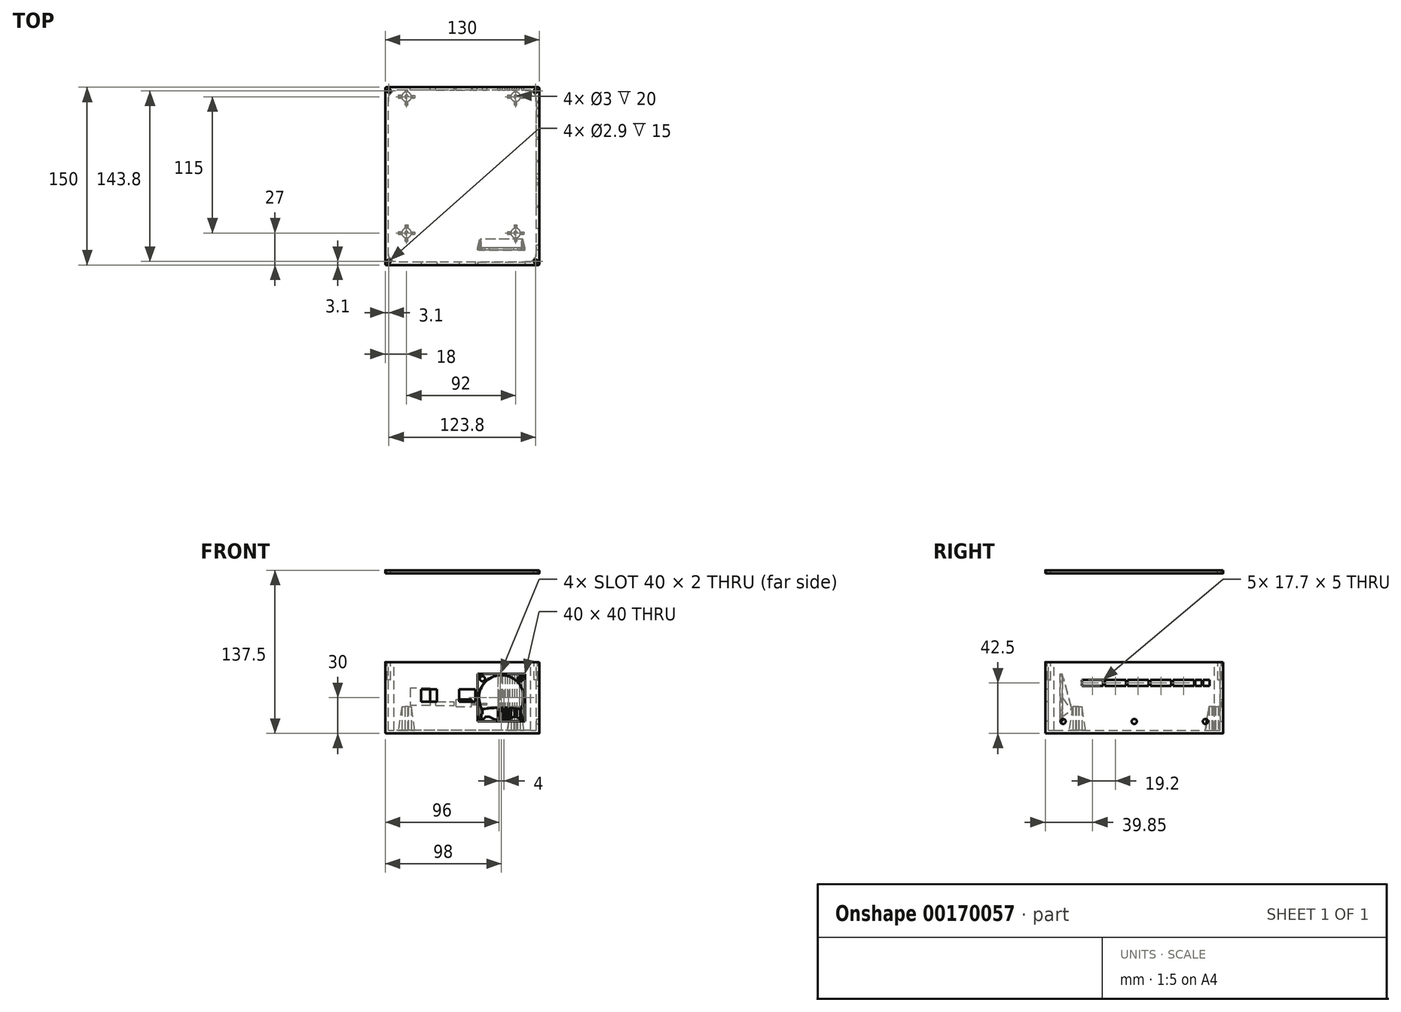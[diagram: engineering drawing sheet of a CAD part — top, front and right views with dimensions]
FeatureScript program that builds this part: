
annotation { "Feature Type Name" : "Feature", "Feature Type Description" : "" }
export const myFeature = defineFeature(function(context is Context, id is Id, definition is map)
    precondition{}
    {
        {
            var Q0;
            Q0=qCreatedBy(makeId("Top.planeOp"),FACE);
            var sketch = newSketch(context, id + "F0", { "sketchPlane" : qUnion([Q0])});
            skLineSegment(sketch, "E0.bottom", {"start": v(65, -75) * mm, "end": v(-65, -75) * mm});
            skLineSegment(sketch, "E0.top", {"start": v(65, 75) * mm, "end": v(-65, 75) * mm});
            skLineSegment(sketch, "E0.left", {"start": v(65, -75) * mm, "end": v(65, 75) * mm});
            skLineSegment(sketch, "E0.right", {"start": v(-65, -75) * mm, "end": v(-65, 75) * mm});
            skPoint(sketch, "E0.middle", {"position": v(0, 0) * mm});
            skCircle(sketch, "E1", {"center": v(-47, 67) * mm, "radius": 1.5 * mm});
            skCircle(sketch, "E2", {"center": v(45, 67) * mm, "radius": 1.5 * mm});
            skCircle(sketch, "E3", {"center": v(45, -48) * mm, "radius": 1.5 * mm});
            skCircle(sketch, "E4", {"center": v(-47, -48) * mm, "radius": 1.5 * mm});
            skCircle(sketch, "E5", {"center": v(-47, -48) * mm, "radius": 4 * mm});
            skCircle(sketch, "E6", {"center": v(45, -48) * mm, "radius": 4 * mm});
            skCircle(sketch, "E7", {"center": v(45, 67) * mm, "radius": 4 * mm});
            skCircle(sketch, "E8", {"center": v(-47, 67) * mm, "radius": 4 * mm});
            skLineSegment(sketch, "E9.bottom", {"start": v(46, 74) * mm, "end": v(44, 74) * mm});
            skLineSegment(sketch, "E9.top", {"start": v(46, 60) * mm, "end": v(44, 60) * mm});
            skLineSegment(sketch, "E9.left", {"start": v(46, 74) * mm, "end": v(46, 70.87) * mm});
            skLineSegment(sketch, "E9.right", {"start": v(44, 74) * mm, "end": v(44, 70.87) * mm});
            skLineSegment(sketch, "E10.bottom", {"start": v(52, 66) * mm, "end": v(48.87, 66) * mm});
            skLineSegment(sketch, "E10.top", {"start": v(52, 68) * mm, "end": v(48.87, 68) * mm});
            skLineSegment(sketch, "E10.left", {"start": v(52, 66) * mm, "end": v(52, 68) * mm});
            skLineSegment(sketch, "E10.right", {"start": v(38, 66) * mm, "end": v(38, 68) * mm});
            skLineSegment(sketch, "E11.trimOffspring", {"start": v(41.13, 68) * mm, "end": v(38, 68) * mm});
            skLineSegment(sketch, "E12.trimOffspring", {"start": v(41.13, 66) * mm, "end": v(38, 66) * mm});
            skLineSegment(sketch, "E13.trimOffspring", {"start": v(44, 63.13) * mm, "end": v(44, 60) * mm});
            skLineSegment(sketch, "E14.trimOffspring", {"start": v(46, 63.13) * mm, "end": v(46, 60) * mm});
            skLineSegment(sketch, "E15.bottom", {"start": v(-40, 66) * mm, "end": v(-43.13, 66) * mm});
            skLineSegment(sketch, "E15.top", {"start": v(-40, 68) * mm, "end": v(-43.13, 68) * mm});
            skLineSegment(sketch, "E15.left", {"start": v(-40, 66) * mm, "end": v(-40, 68) * mm});
            skLineSegment(sketch, "E15.right", {"start": v(-54, 66) * mm, "end": v(-54, 68) * mm});
            skLineSegment(sketch, "E16.bottom", {"start": v(-46, 74) * mm, "end": v(-48, 74) * mm});
            skLineSegment(sketch, "E16.top", {"start": v(-46, 60) * mm, "end": v(-48, 60) * mm});
            skLineSegment(sketch, "E16.left", {"start": v(-46, 74) * mm, "end": v(-46, 70.87) * mm});
            skLineSegment(sketch, "E16.right", {"start": v(-48, 74) * mm, "end": v(-48, 70.87) * mm});
            skLineSegment(sketch, "E17.trimOffspring", {"start": v(-50.87, 68) * mm, "end": v(-54, 68) * mm});
            skLineSegment(sketch, "E18.trimOffspring", {"start": v(-50.87, 66) * mm, "end": v(-54, 66) * mm});
            skLineSegment(sketch, "E19.trimOffspring", {"start": v(-48, 63.13) * mm, "end": v(-48, 60) * mm});
            skLineSegment(sketch, "E20.trimOffspring", {"start": v(-46, 63.13) * mm, "end": v(-46, 60) * mm});
            skLineSegment(sketch, "E21.bottom", {"start": v(-40, -49) * mm, "end": v(-43.13, -49) * mm});
            skLineSegment(sketch, "E21.top", {"start": v(-40, -47) * mm, "end": v(-43.13, -47) * mm});
            skLineSegment(sketch, "E21.left", {"start": v(-40, -49) * mm, "end": v(-40, -47) * mm});
            skLineSegment(sketch, "E21.right", {"start": v(-54, -49) * mm, "end": v(-54, -47) * mm});
            skLineSegment(sketch, "E22.bottom", {"start": v(-46, -41) * mm, "end": v(-48, -41) * mm});
            skLineSegment(sketch, "E22.top", {"start": v(-46, -55) * mm, "end": v(-48, -55) * mm});
            skLineSegment(sketch, "E22.left", {"start": v(-46, -41) * mm, "end": v(-46, -44.13) * mm});
            skLineSegment(sketch, "E22.right", {"start": v(-48, -41) * mm, "end": v(-48, -44.13) * mm});
            skLineSegment(sketch, "E23.trimOffspring", {"start": v(-50.87, -49) * mm, "end": v(-54, -49) * mm});
            skLineSegment(sketch, "E24.trimOffspring", {"start": v(-50.87, -47) * mm, "end": v(-54, -47) * mm});
            skLineSegment(sketch, "E25.trimOffspring", {"start": v(-46, -51.87) * mm, "end": v(-46, -55) * mm});
            skLineSegment(sketch, "E26.trimOffspring", {"start": v(-48, -51.87) * mm, "end": v(-48, -55) * mm});
            skLineSegment(sketch, "E27.bottom", {"start": v(52, -49) * mm, "end": v(48.87, -49) * mm});
            skLineSegment(sketch, "E27.top", {"start": v(52, -47) * mm, "end": v(48.87, -47) * mm});
            skLineSegment(sketch, "E27.left", {"start": v(52, -49) * mm, "end": v(52, -47) * mm});
            skLineSegment(sketch, "E27.right", {"start": v(38, -49) * mm, "end": v(38, -47) * mm});
            skLineSegment(sketch, "E28.bottom", {"start": v(46, -55) * mm, "end": v(44, -55) * mm});
            skLineSegment(sketch, "E28.top", {"start": v(46, -41) * mm, "end": v(44, -41) * mm});
            skLineSegment(sketch, "E28.left", {"start": v(46, -55) * mm, "end": v(46, -51.87) * mm});
            skLineSegment(sketch, "E28.right", {"start": v(44, -55) * mm, "end": v(44, -51.87) * mm});
            skLineSegment(sketch, "E29.trimOffspring", {"start": v(41.13, -49) * mm, "end": v(38, -49) * mm});
            skLineSegment(sketch, "E30.trimOffspring", {"start": v(41.13, -47) * mm, "end": v(38, -47) * mm});
            skLineSegment(sketch, "E31.trimOffspring", {"start": v(44, -44.13) * mm, "end": v(44, -41) * mm});
            skLineSegment(sketch, "E32.trimOffspring", {"start": v(46, -44.13) * mm, "end": v(46, -41) * mm});
            skLineSegment(sketch, "E33", {"start": v(65, 65) * mm, "end": v(55, 75) * mm});
            skLineSegment(sketch, "E34", {"start": v(65, -65) * mm, "end": v(55, -75) * mm});
            skLineSegment(sketch, "E35", {"start": v(-55, 75) * mm, "end": v(-65, 65) * mm});
            skLineSegment(sketch, "E36", {"start": v(-65, -65) * mm, "end": v(-55, -75) * mm});
            skSolve(sketch);
        }
        {
            var Q0;
            Q0=makeQuery(id+"F0.imprint","IMPRINT",FACE,{"disambiguationData":[TD([[makeQuery(id+"F0.imprint","IMPRINT",EDGE,{"derivedFrom":sQuery(id+"F0.wireOp",EDGE,"E0.bottom")}),-1.0]])]});
            var Q1;
            Q1=makeQuery(id+"F0.imprint","IMPRINT",FACE,{"disambiguationData":[TD([[makeQuery(id+"F0.imprint","IMPRINT",EDGE,{"derivedFrom":sQuery(id+"F0.wireOp",EDGE,"E2")}),-1.0]])]});
            var Q2;
            Q2=makeQuery(id+"F0.imprint","IMPRINT",FACE,{"disambiguationData":[TD([[makeQuery(id+"F0.imprint","IMPRINT",EDGE,{"derivedFrom":sQuery(id+"F0.wireOp",EDGE,"E4")}),-1.0]])]});
            var Q3;
            Q3=makeQuery(id+"F0.imprint","IMPRINT",FACE,{"disambiguationData":[TD([[makeQuery(id+"F0.imprint","IMPRINT",EDGE,{"derivedFrom":sQuery(id+"F0.wireOp",EDGE,"E16.top")}),-1.0]])]});
            var Q4;
            Q4=makeQuery(id+"F0.imprint","IMPRINT",FACE,{"disambiguationData":[TD([[makeQuery(id+"F0.imprint","IMPRINT",EDGE,{"derivedFrom":sQuery(id+"F0.wireOp",EDGE,"E21.right")}),-1.0]])]});
            var Q5;
            Q5=makeQuery(id+"F0.imprint","IMPRINT",FACE,{"disambiguationData":[TD([[makeQuery(id+"F0.imprint","IMPRINT",EDGE,{"derivedFrom":sQuery(id+"F0.wireOp",EDGE,"E22.top")}),-1.0]])]});
            var Q6;
            Q6=makeQuery(id+"F0.imprint","IMPRINT",FACE,{"disambiguationData":[TD([[makeQuery(id+"F0.imprint","IMPRINT",EDGE,{"derivedFrom":sQuery(id+"F0.wireOp",EDGE,"E1")}),-1.0]])]});
            var Q7;
            Q7=makeQuery(id+"F0.imprint","IMPRINT",FACE,{"disambiguationData":[TD([[makeQuery(id+"F0.imprint","IMPRINT",EDGE,{"derivedFrom":sQuery(id+"F0.wireOp",EDGE,"E3")}),-1.0]])]});
            var Q8;
            Q8=makeQuery(id+"F0.imprint","IMPRINT",FACE,{"disambiguationData":[TD([[makeQuery(id+"F0.imprint","IMPRINT",EDGE,{"derivedFrom":sQuery(id+"F0.wireOp",EDGE,"E15.right")}),-1.0]])]});
            var Q9;
            Q9=makeQuery(id+"F0.imprint","IMPRINT",FACE,{"disambiguationData":[TD([[makeQuery(id+"F0.imprint","IMPRINT",EDGE,{"derivedFrom":sQuery(id+"F0.wireOp",EDGE,"E28.bottom")}),-1.0]])]});
            var Q10;
            {var subQ0=sQuery(id+"F0.wireOp",EDGE,"E10.bottom");Q10=makeQuery(id+"F0.imprint","IMPRINT",FACE,{"disambiguationData":[TD([[makeQuery(id+"F0.imprint","IMPRINT",EDGE,{"derivedFrom":subQ0}),-1.0]])]});}
            var Q11;
            Q11=makeQuery(id+"F0.imprint","IMPRINT",FACE,{"disambiguationData":[TD([[makeQuery(id+"F0.imprint","IMPRINT",EDGE,{"derivedFrom":sQuery(id+"F0.wireOp",EDGE,"E9.top")}),-1.0]])]});
            var Q12;
            {var subQ0=sQuery(id+"F0.wireOp",EDGE,"E21.bottom");Q12=makeQuery(id+"F0.imprint","IMPRINT",FACE,{"disambiguationData":[TD([[makeQuery(id+"F0.imprint","IMPRINT",EDGE,{"derivedFrom":subQ0}),-1.0]])]});}
            var Q13;
            Q13=makeQuery(id+"F0.imprint","IMPRINT",FACE,{"disambiguationData":[TD([[makeQuery(id+"F0.imprint","IMPRINT",EDGE,{"derivedFrom":sQuery(id+"F0.wireOp",EDGE,"E28.top")}),1.0]])]});
            var Q14;
            Q14=makeQuery(id+"F0.imprint","IMPRINT",FACE,{"disambiguationData":[TD([[makeQuery(id+"F0.imprint","IMPRINT",EDGE,{"derivedFrom":sQuery(id+"F0.wireOp",EDGE,"E27.right")}),-1.0]])]});
            var Q15;
            Q15=makeQuery(id+"F0.imprint","IMPRINT",FACE,{"disambiguationData":[TD([[makeQuery(id+"F0.imprint","IMPRINT",EDGE,{"derivedFrom":sQuery(id+"F0.wireOp",EDGE,"E22.bottom")}),1.0]])]});
            var Q16;
            {var subQ0=sQuery(id+"F0.wireOp",EDGE,"E15.bottom");Q16=makeQuery(id+"F0.imprint","IMPRINT",FACE,{"disambiguationData":[TD([[makeQuery(id+"F0.imprint","IMPRINT",EDGE,{"derivedFrom":subQ0}),-1.0]])]});}
            var Q17;
            Q17=makeQuery(id+"F0.imprint","IMPRINT",FACE,{"disambiguationData":[TD([[makeQuery(id+"F0.imprint","IMPRINT",EDGE,{"derivedFrom":sQuery(id+"F0.wireOp",EDGE,"E9.bottom")}),1.0]])]});
            var Q18;
            {var subQ0=sQuery(id+"F0.wireOp",EDGE,"E27.bottom");Q18=makeQuery(id+"F0.imprint","IMPRINT",FACE,{"disambiguationData":[TD([[makeQuery(id+"F0.imprint","IMPRINT",EDGE,{"derivedFrom":subQ0}),-1.0]])]});}
            var Q19;
            Q19=makeQuery(id+"F0.imprint","IMPRINT",FACE,{"disambiguationData":[TD([[makeQuery(id+"F0.imprint","IMPRINT",EDGE,{"derivedFrom":sQuery(id+"F0.wireOp",EDGE,"E10.right")}),-1.0]])]});
            var Q20;
            Q20=makeQuery(id+"F0.imprint","IMPRINT",FACE,{"disambiguationData":[TD([[makeQuery(id+"F0.imprint","IMPRINT",EDGE,{"derivedFrom":sQuery(id+"F0.wireOp",EDGE,"E16.bottom")}),1.0]])]});
            var Q21;
            Q21=makeQuery(id+"F0.imprint","IMPRINT",FACE,{"disambiguationData":[TD([[makeQuery(id+"F0.imprint","IMPRINT",EDGE,{"derivedFrom":sQuery(id+"F0.wireOp",EDGE,"E2")}),1.0]])]});
            var Q22;
            Q22=makeQuery(id+"F0.imprint","IMPRINT",FACE,{"disambiguationData":[TD([[makeQuery(id+"F0.imprint","IMPRINT",EDGE,{"derivedFrom":sQuery(id+"F0.wireOp",EDGE,"E1")}),1.0]])]});
            var Q23;
            Q23=makeQuery(id+"F0.imprint","IMPRINT",FACE,{"disambiguationData":[TD([[makeQuery(id+"F0.imprint","IMPRINT",EDGE,{"derivedFrom":sQuery(id+"F0.wireOp",EDGE,"E4")}),1.0]])]});
            var Q24;
            Q24=makeQuery(id+"F0.imprint","IMPRINT",FACE,{"disambiguationData":[TD([[makeQuery(id+"F0.imprint","IMPRINT",EDGE,{"derivedFrom":sQuery(id+"F0.wireOp",EDGE,"E3")}),1.0]])]});
            var Q25;
            Q25=makeQuery(id+"F0.imprint","IMPRINT",FACE,{"disambiguationData":[TD([[makeQuery(id+"F0.imprint","IMPRINT",EDGE,{"derivedFrom":sQuery(id+"F0.wireOp",EDGE,"E9.bottom")}),-1.0]])]});
            var Q26;
            {var subQ3=sQuery(id+"F0.wireOp",EDGE,"E33");Q26=makeQuery(id+"F0.imprint","IMPRINT",FACE,{"disambiguationData":[TD([[makeQuery(id+"F0.imprint","IMPRINT",EDGE,{"derivedFrom":subQ3}),-1.0]])]});}
            var Q27;
            {var subQ3=sQuery(id+"F0.wireOp",EDGE,"E35");Q27=makeQuery(id+"F0.imprint","IMPRINT",FACE,{"disambiguationData":[TD([[makeQuery(id+"F0.imprint","IMPRINT",EDGE,{"derivedFrom":subQ3}),-1.0]])]});}
            extrude(context, id + "F1", {"entities" : qUnion([Q0, Q1, Q2, Q3, Q4, Q5, Q6, Q7, Q8, Q9, Q10, Q11, Q12, Q13, Q14, Q15, Q16, Q17, Q18, Q19, Q20, Q21, Q22, Q23, Q24, Q25, Q26, Q27]), "depth" : 60 * mm});
        }
        {
            var Q0;
            Q0=makeQuery(id+"F1.opExtrude","CAP_FACE",FACE,{"disambiguationData":[OSD([sQuery(id+"F0.wireOp",EDGE,"E0.bottom"),sQuery(id+"F0.wireOp",EDGE,"E0.top"),sQuery(id+"F0.wireOp",EDGE,"E0.left"),sQuery(id+"F0.wireOp",EDGE,"E0.right")])],"isStart":false});
            shell(context, id + "F2", {"entities" : qUnion([Q0]), "thickness" : 2.5 * mm});
        }
        {
            var Q0;
            Q0=makeQuery(id+"F0.imprint","IMPRINT",FACE,{"disambiguationData":[TD([[makeQuery(id+"F0.imprint","IMPRINT",EDGE,{"derivedFrom":sQuery(id+"F0.wireOp",EDGE,"E1")}),-1.0]])]});
            var Q1;
            Q1=makeQuery(id+"F0.imprint","IMPRINT",FACE,{"disambiguationData":[TD([[makeQuery(id+"F0.imprint","IMPRINT",EDGE,{"derivedFrom":sQuery(id+"F0.wireOp",EDGE,"E4")}),-1.0]])]});
            var Q2;
            Q2=makeQuery(id+"F0.imprint","IMPRINT",FACE,{"disambiguationData":[TD([[makeQuery(id+"F0.imprint","IMPRINT",EDGE,{"derivedFrom":sQuery(id+"F0.wireOp",EDGE,"E3")}),-1.0]])]});
            var Q3;
            Q3=makeQuery(id+"F0.imprint","IMPRINT",FACE,{"disambiguationData":[TD([[makeQuery(id+"F0.imprint","IMPRINT",EDGE,{"derivedFrom":sQuery(id+"F0.wireOp",EDGE,"E2")}),-1.0]])]});
            var Q4;
            {var subQ0=sQuery(id+"F0.wireOp",EDGE,"E10.bottom");Q4=makeQuery(id+"F0.imprint","IMPRINT",FACE,{"disambiguationData":[TD([[makeQuery(id+"F0.imprint","IMPRINT",EDGE,{"derivedFrom":subQ0}),-1.0]])]});}
            var Q5;
            Q5=makeQuery(id+"F0.imprint","IMPRINT",FACE,{"disambiguationData":[TD([[makeQuery(id+"F0.imprint","IMPRINT",EDGE,{"derivedFrom":sQuery(id+"F0.wireOp",EDGE,"E9.top")}),-1.0]])]});
            var Q6;
            Q6=makeQuery(id+"F0.imprint","IMPRINT",FACE,{"disambiguationData":[TD([[makeQuery(id+"F0.imprint","IMPRINT",EDGE,{"derivedFrom":sQuery(id+"F0.wireOp",EDGE,"E10.right")}),-1.0]])]});
            var Q7;
            Q7=makeQuery(id+"F0.imprint","IMPRINT",FACE,{"disambiguationData":[TD([[makeQuery(id+"F0.imprint","IMPRINT",EDGE,{"derivedFrom":sQuery(id+"F0.wireOp",EDGE,"E9.bottom")}),1.0]])]});
            var Q8;
            Q8=makeQuery(id+"F0.imprint","IMPRINT",FACE,{"disambiguationData":[TD([[makeQuery(id+"F0.imprint","IMPRINT",EDGE,{"derivedFrom":sQuery(id+"F0.wireOp",EDGE,"E16.bottom")}),1.0]])]});
            var Q9;
            Q9=makeQuery(id+"F0.imprint","IMPRINT",FACE,{"disambiguationData":[TD([[makeQuery(id+"F0.imprint","IMPRINT",EDGE,{"derivedFrom":sQuery(id+"F0.wireOp",EDGE,"E15.right")}),-1.0]])]});
            var Q10;
            Q10=makeQuery(id+"F0.imprint","IMPRINT",FACE,{"disambiguationData":[TD([[makeQuery(id+"F0.imprint","IMPRINT",EDGE,{"derivedFrom":sQuery(id+"F0.wireOp",EDGE,"E16.top")}),-1.0]])]});
            var Q11;
            {var subQ0=sQuery(id+"F0.wireOp",EDGE,"E15.bottom");Q11=makeQuery(id+"F0.imprint","IMPRINT",FACE,{"disambiguationData":[TD([[makeQuery(id+"F0.imprint","IMPRINT",EDGE,{"derivedFrom":subQ0}),-1.0]])]});}
            var Q12;
            {var subQ0=sQuery(id+"F0.wireOp",EDGE,"E21.bottom");Q12=makeQuery(id+"F0.imprint","IMPRINT",FACE,{"disambiguationData":[TD([[makeQuery(id+"F0.imprint","IMPRINT",EDGE,{"derivedFrom":subQ0}),-1.0]])]});}
            var Q13;
            Q13=makeQuery(id+"F0.imprint","IMPRINT",FACE,{"disambiguationData":[TD([[makeQuery(id+"F0.imprint","IMPRINT",EDGE,{"derivedFrom":sQuery(id+"F0.wireOp",EDGE,"E22.bottom")}),1.0]])]});
            var Q14;
            Q14=makeQuery(id+"F0.imprint","IMPRINT",FACE,{"disambiguationData":[TD([[makeQuery(id+"F0.imprint","IMPRINT",EDGE,{"derivedFrom":sQuery(id+"F0.wireOp",EDGE,"E21.right")}),-1.0]])]});
            var Q15;
            Q15=makeQuery(id+"F0.imprint","IMPRINT",FACE,{"disambiguationData":[TD([[makeQuery(id+"F0.imprint","IMPRINT",EDGE,{"derivedFrom":sQuery(id+"F0.wireOp",EDGE,"E22.top")}),-1.0]])]});
            var Q16;
            Q16=makeQuery(id+"F0.imprint","IMPRINT",FACE,{"disambiguationData":[TD([[makeQuery(id+"F0.imprint","IMPRINT",EDGE,{"derivedFrom":sQuery(id+"F0.wireOp",EDGE,"E27.right")}),-1.0]])]});
            var Q17;
            Q17=makeQuery(id+"F0.imprint","IMPRINT",FACE,{"disambiguationData":[TD([[makeQuery(id+"F0.imprint","IMPRINT",EDGE,{"derivedFrom":sQuery(id+"F0.wireOp",EDGE,"E28.top")}),1.0]])]});
            var Q18;
            {var subQ0=sQuery(id+"F0.wireOp",EDGE,"E27.bottom");Q18=makeQuery(id+"F0.imprint","IMPRINT",FACE,{"disambiguationData":[TD([[makeQuery(id+"F0.imprint","IMPRINT",EDGE,{"derivedFrom":subQ0}),-1.0]])]});}
            var Q19;
            Q19=makeQuery(id+"F0.imprint","IMPRINT",FACE,{"disambiguationData":[TD([[makeQuery(id+"F0.imprint","IMPRINT",EDGE,{"derivedFrom":sQuery(id+"F0.wireOp",EDGE,"E28.bottom")}),-1.0]])]});
            extrude(context, id + "F3", {"entities" : qUnion([Q0, Q1, Q2, Q3, Q4, Q5, Q6, Q7, Q8, Q9, Q10, Q11, Q12, Q13, Q14, Q15, Q16, Q17, Q18, Q19]), "operationType" : NewBodyOperationType.ADD, "depth" : (20 + 2.5) * mm});
        }
        {
            var Q0;
            Q0=makeQuery(id+"F1.opExtrude","SWEPT_FACE",FACE,{"disambiguationData":[OSD([sQuery(id+"F0.wireOp",EDGE,"E0.top")])]});
            var sketch = newSketch(context, id + "F4", { "sketchPlane" : qUnion([Q0])});
            skLineSegment(sketch, "E37.bottom", {"start": v(27, 38) * mm, "end": v(44, 38) * mm});
            skLineSegment(sketch, "E37.top", {"start": v(27, 23.5) * mm, "end": v(44, 23.5) * mm});
            skLineSegment(sketch, "E37.left", {"start": v(27, 38) * mm, "end": v(27, 23.5) * mm});
            skLineSegment(sketch, "E37.right", {"start": v(44, 38) * mm, "end": v(44, 23.5) * mm});
            skLineSegment(sketch, "E38.bottom", {"start": v(22.5, 23.5) * mm, "end": v(6.7, 23.5) * mm});
            skLineSegment(sketch, "E38.top", {"start": v(22.5, 26.5) * mm, "end": v(6.7, 26.5) * mm});
            skLineSegment(sketch, "E38.left", {"start": v(22.5, 23.5) * mm, "end": v(22.5, 26.5) * mm});
            skLineSegment(sketch, "E38.right", {"start": v(6.7, 23.5) * mm, "end": v(6.7, 26.5) * mm});
            skLineSegment(sketch, "E39.bottom", {"start": v(5.25, 22.4) * mm, "end": v(-7.75, 22.4) * mm});
            skLineSegment(sketch, "E39.top", {"start": v(5.25, 28.4) * mm, "end": v(-7.75, 28.4) * mm});
            skLineSegment(sketch, "E39.left", {"start": v(5.25, 22.4) * mm, "end": v(5.25, 28.4) * mm});
            skLineSegment(sketch, "E39.right", {"start": v(-7.75, 22.4) * mm, "end": v(-7.75, 28.4) * mm});
            skLineSegment(sketch, "E40.bottom", {"start": v(-8.65, 24) * mm, "end": v(-12.65, 24) * mm});
            skLineSegment(sketch, "E40.top", {"start": v(-8.65, 25.45) * mm, "end": v(-12.65, 25.45) * mm});
            skLineSegment(sketch, "E40.left", {"start": v(-8.65, 24) * mm, "end": v(-8.65, 25.45) * mm});
            skLineSegment(sketch, "E40.right", {"start": v(-12.65, 24) * mm, "end": v(-12.65, 25.45) * mm});
            skLineSegment(sketch, "E41.bottom", {"start": v(-16.95, 24) * mm, "end": v(-20.95, 24) * mm});
            skLineSegment(sketch, "E41.top", {"start": v(-16.95, 25.45) * mm, "end": v(-20.95, 25.45) * mm});
            skLineSegment(sketch, "E41.left", {"start": v(-16.95, 24) * mm, "end": v(-16.95, 25.45) * mm});
            skLineSegment(sketch, "E41.right", {"start": v(-20.95, 24) * mm, "end": v(-20.95, 25.45) * mm});
            skSolve(sketch);
        }
        {
            var Q0;
            Q0=qSketchRegion(id+"F4",true);
            extrude(context, id + "F5", {"entities" : qUnion([Q0]), "operationType" : NewBodyOperationType.REMOVE, "endBound" : BoundingType.UP_TO_NEXT, "oppositeDirection" : true, "depth" : 25 * mm});
        }
        {
            var Q0;
            Q0=makeQuery(id+"F1.opExtrude","SWEPT_FACE",FACE,{"disambiguationData":[OSD([sQuery(id+"F0.wireOp",EDGE,"E0.bottom")])]});
            var sketch = newSketch(context, id + "F6", { "sketchPlane" : qUnion([Q0])});
            skCircle(sketch, "E42", {"center": v(33, 30) * mm, "radius": 19 * mm});
            skPoint(sketch, "E42.centerSnap0", {"position": v(13, 30) * mm});
            skPoint(sketch, "E42.centerSnap1", {"position": v(33, 50) * mm});
            skCircle(sketch, "E43", {"center": v(17, 46) * mm, "radius": 2 * mm});
            skCircle(sketch, "E44", {"center": v(49, 46) * mm, "radius": 2 * mm});
            skCircle(sketch, "E45", {"center": v(49, 14) * mm, "radius": 2 * mm});
            skCircle(sketch, "E46", {"center": v(17, 14) * mm, "radius": 2 * mm});
            skLineSegment(sketch, "E47.bottom", {"start": v(17, 14) * mm, "end": v(49, 14) * mm, "construction": true});
            skLineSegment(sketch, "E47.top", {"start": v(17, 46) * mm, "end": v(49, 46) * mm, "construction": true});
            skLineSegment(sketch, "E47.left", {"start": v(17, 14) * mm, "end": v(17, 46) * mm, "construction": true});
            skLineSegment(sketch, "E47.right", {"start": v(49, 14) * mm, "end": v(49, 46) * mm, "construction": true});
            skLineSegment(sketch, "E48.bottom", {"start": v(-2.63, 37) * mm, "end": v(10.87, 37) * mm});
            skLineSegment(sketch, "E48.top", {"start": v(-2.63, 26.5) * mm, "end": v(10.87, 26.5) * mm});
            skLineSegment(sketch, "E48.left", {"start": v(-2.63, 37) * mm, "end": v(-2.63, 26.5) * mm});
            skLineSegment(sketch, "E48.right", {"start": v(10.87, 37) * mm, "end": v(10.87, 26.5) * mm});
            skLineSegment(sketch, "E49.bottom", {"start": v(-34.88, 37) * mm, "end": v(-21.38, 37) * mm});
            skLineSegment(sketch, "E49.top", {"start": v(-34.88, 26.5) * mm, "end": v(-21.38, 26.5) * mm});
            skLineSegment(sketch, "E49.left", {"start": v(-34.88, 37) * mm, "end": v(-34.88, 26.5) * mm});
            skLineSegment(sketch, "E49.right", {"start": v(-21.38, 37) * mm, "end": v(-21.38, 26.5) * mm});
            skSolve(sketch);
        }
        {
            var Q0;
            Q0=qSketchRegion(id+"F6",true);
            extrude(context, id + "F7", {"entities" : qUnion([Q0]), "operationType" : NewBodyOperationType.REMOVE, "endBound" : BoundingType.UP_TO_NEXT, "oppositeDirection" : true, "depth" : 25 * mm});
        }
        {
            var Q0;
            Q0=makeQuery(id+"F1.opExtrude","SWEPT_FACE",FACE,{"disambiguationData":[OSD([sQuery(id+"F0.wireOp",EDGE,"E0.left")])]});
            var sketch = newSketch(context, id + "F8", { "sketchPlane" : qUnion([Q0])});
            skLineSegment(sketch, "E50.bottom", {"start": v(-75, 0) * mm, "end": v(75, 0) * mm, "construction": true});
            skLineSegment(sketch, "E50.top", {"start": v(-75, 20) * mm, "end": v(75, 20) * mm, "construction": true});
            skLineSegment(sketch, "E50.left", {"start": v(-75, 0) * mm, "end": v(-75, 20) * mm, "construction": true});
            skLineSegment(sketch, "E50.right", {"start": v(75, 0) * mm, "end": v(75, 20) * mm, "construction": true});
            skCircle(sketch, "E51", {"center": v(-60, 10) * mm, "radius": 2.15 * mm});
            skPoint(sketch, "E51.centerSnap0", {"position": v(-75, 10) * mm});
            skCircle(sketch, "E52", {"center": v(60, 10) * mm, "radius": 2.15 * mm});
            skCircle(sketch, "E53", {"center": v(0, 10) * mm, "radius": 2.15 * mm});
            skPoint(sketch, "E53.centerSnap0", {"position": v(0, 0) * mm});
            skPoint(sketch, "E54.firstSnap0", {"position": v(-75, 40) * mm});
            skLineSegment(sketch, "E54.bottom", {"start": v(-44, 40) * mm, "end": v(-26.3, 40) * mm});
            skLineSegment(sketch, "E54.top", {"start": v(-44, 45) * mm, "end": v(-26.3, 45) * mm});
            skLineSegment(sketch, "E54.left", {"start": v(-44, 40) * mm, "end": v(-44, 45) * mm});
            skLineSegment(sketch, "E54.right", {"start": v(63.5, 40) * mm, "end": v(63.5, 45) * mm});
            skLineSegment(sketch, "E55.bottom", {"start": v(63.5, 45) * mm, "end": v(58, 45) * mm});
            skLineSegment(sketch, "E55.top", {"start": v(63.5, 40) * mm, "end": v(58, 40) * mm});
            skLineSegment(sketch, "E55.left", {"start": v(63.5, 45) * mm, "end": v(63.5, 40) * mm});
            skLineSegment(sketch, "E55.right", {"start": v(58, 45) * mm, "end": v(58, 40) * mm});
            skLineSegment(sketch, "E56.bottom", {"start": v(57, 45) * mm, "end": v(51.5, 45) * mm});
            skLineSegment(sketch, "E56.top", {"start": v(57, 40) * mm, "end": v(51.5, 40) * mm});
            skLineSegment(sketch, "E56.left", {"start": v(57, 45) * mm, "end": v(57, 40) * mm});
            skLineSegment(sketch, "E56.right", {"start": v(51.5, 45) * mm, "end": v(51.5, 40) * mm});
            skLineSegment(sketch, "E57.trimOffspring", {"start": v(58, 45) * mm, "end": v(63.5, 45) * mm});
            skLineSegment(sketch, "E58.trimOffspring", {"start": v(58, 40) * mm, "end": v(63.5, 40) * mm});
            skLineSegment(sketch, "E59", {"start": v(50.5, 45) * mm, "end": v(50.5, 40) * mm});
            skLineSegment(sketch, "E60.trimOffspring", {"start": v(51.5, 45) * mm, "end": v(57, 45) * mm});
            skLineSegment(sketch, "E61.trimOffspring", {"start": v(51.5, 40) * mm, "end": v(57, 40) * mm});
            skLineSegment(sketch, "E62.left", {"start": v(31.3, 45) * mm, "end": v(31.3, 40) * mm});
            skLineSegment(sketch, "E62.right", {"start": v(32.8, 45) * mm, "end": v(32.8, 40) * mm});
            skLineSegment(sketch, "E63.trimOffspring", {"start": v(32.8, 45) * mm, "end": v(50.5, 45) * mm});
            skLineSegment(sketch, "E64.trimOffspring", {"start": v(32.8, 40) * mm, "end": v(50.5, 40) * mm});
            skLineSegment(sketch, "E65.left", {"start": v(12.1, 45) * mm, "end": v(12.1, 40) * mm});
            skLineSegment(sketch, "E65.right", {"start": v(13.6, 45) * mm, "end": v(13.6, 40) * mm});
            skLineSegment(sketch, "E66.left", {"start": v(-7.1, 45) * mm, "end": v(-7.1, 40) * mm});
            skLineSegment(sketch, "E66.right", {"start": v(-5.6, 45) * mm, "end": v(-5.6, 40) * mm});
            skLineSegment(sketch, "E67.trimOffspring", {"start": v(-5.6, 45) * mm, "end": v(12.1, 45) * mm});
            skLineSegment(sketch, "E68.trimOffspring", {"start": v(-5.6, 40) * mm, "end": v(12.1, 40) * mm});
            skLineSegment(sketch, "E69.trimOffspring", {"start": v(13.6, 45) * mm, "end": v(31.3, 45) * mm});
            skLineSegment(sketch, "E70.trimOffspring", {"start": v(13.6, 40) * mm, "end": v(31.3, 40) * mm});
            skLineSegment(sketch, "E71.left", {"start": v(-26.3, 45) * mm, "end": v(-26.3, 40) * mm});
            skLineSegment(sketch, "E71.right", {"start": v(-24.8, 45) * mm, "end": v(-24.8, 40) * mm});
            skLineSegment(sketch, "E72.trimOffspring", {"start": v(-24.8, 45) * mm, "end": v(-7.1, 45) * mm});
            skLineSegment(sketch, "E73.trimOffspring", {"start": v(-24.8, 40) * mm, "end": v(-7.1, 40) * mm});
            skLineSegment(sketch, "E74", {"start": v(-44, 45) * mm, "end": v(12.1, 45) * mm, "construction": true});
            skLineSegment(sketch, "E75", {"start": v(12.1, 40) * mm, "end": v(-44, 40) * mm, "construction": true});
            skLineSegment(sketch, "E76", {"start": v(13.6, 40) * mm, "end": v(63.5, 40) * mm, "construction": true});
            skLineSegment(sketch, "E77", {"start": v(63.5, 45) * mm, "end": v(13.6, 45) * mm, "construction": true});
            skSolve(sketch);
        }
        {
            var Q0;
            Q0=qSketchRegion(id+"F8",true);
            extrude(context, id + "F9", {"entities" : qUnion([Q0]), "operationType" : NewBodyOperationType.REMOVE, "endBound" : BoundingType.UP_TO_NEXT, "oppositeDirection" : true, "depth" : 25 * mm});
        }
        {
            var Q0;
            {var subQ0=sQuery(id+"F0.wireOp",EDGE,"E0.right");var subQ1=sQuery(id+"F0.wireOp",EDGE,"E0.left");var subQ2=sQuery(id+"F0.wireOp",EDGE,"E0.top");var subQ3=sQuery(id+"F0.wireOp",EDGE,"E0.bottom");Q0=makeQuery(id+"F3.boolean.opBoolean","SPLIT",FACE,{"disambiguationData":[TD([makeQuery(id+"F2.opShell","OFFSET_FACE",FACE,{"disambiguationData":[OSD([subQ3])]})])],"derivedFrom":makeQuery(id+"F2.opShell","OFFSET_FACE",FACE,{"disambiguationData":[OSD([subQ3,subQ2,subQ1,subQ0])]})});}
            var sketch = newSketch(context, id + "F10", { "sketchPlane" : qUnion([Q0])});
            skArc(sketch, "E78", {"start": v(57.5, 17.5) * mm, "mid": v(45.78, 45.78) * mm, "end": v(17.5, 57.5) * mm});
            skArc(sketch, "E79.0", {"start": v(55.5, 17.5) * mm, "mid": v(44.37, 44.37) * mm, "end": v(17.5, 55.5) * mm});
            skLineSegment(sketch, "E80", {"start": v(17.5, 57.5) * mm, "end": v(17.5, 55.5) * mm});
            skLineSegment(sketch, "E81", {"start": v(55.5, 17.5) * mm, "end": v(57.5, 17.5) * mm});
            skSolve(sketch);
        }
        {
            var Q0;
            Q0=makeQuery(id+"F1.opExtrude","SWEPT_FACE",FACE,{"disambiguationData":[OSD([sQuery(id+"F0.wireOp",EDGE,"E0.top")])]});
            var sketch = newSketch(context, id + "F11", { "sketchPlane" : qUnion([Q0])});
            skLineSegment(sketch, "E82.bottom", {"start": v(-51, 50) * mm, "end": v(-51, 50) * mm});
            skLineSegment(sketch, "E82.top", {"start": v(-51, 10) * mm, "end": v(-51, 10) * mm});
            skLineSegment(sketch, "E82.left", {"start": v(-52, 49) * mm, "end": v(-52, 11) * mm});
            skLineSegment(sketch, "E82.right", {"start": v(-50, 49) * mm, "end": v(-50, 11) * mm});
            skPoint(sketch, "E83.visualSharp", {"position": v(-52, 50) * mm});
            skArc(sketch, "E83.filletArc", {"start": v(-51, 50) * mm, "mid": v(-51.7, 49.7) * mm, "end": v(-52, 49) * mm});
            skArc(sketch, "E84.filletArc", {"start": v(-50, 49) * mm, "mid": v(-50.3, 49.7) * mm, "end": v(-51, 50) * mm});
            skPoint(sketch, "E85.visualSharp", {"position": v(-52, 10) * mm});
            skArc(sketch, "E85.filletArc", {"start": v(-52, 11) * mm, "mid": v(-51.7, 10.3) * mm, "end": v(-51, 10) * mm});
            skPoint(sketch, "E86.visualSharp", {"position": v(-50, 10) * mm});
            skArc(sketch, "E86.filletArc", {"start": v(-51, 10) * mm, "mid": v(-50.3, 10.3) * mm, "end": v(-50, 11) * mm});
            skPoint(sketch, "E87.1.0.0", {"position": v(-46, 10) * mm});
            skPoint(sketch, "E87.1.0.1", {"position": v(-48, 10) * mm});
            skPoint(sketch, "E87.1.0.2", {"position": v(-48, 50) * mm});
            skLineSegment(sketch, "E87.1.0.3", {"start": v(-48, 49) * mm, "end": v(-48, 11) * mm});
            skLineSegment(sketch, "E87.1.0.4", {"start": v(-46, 49) * mm, "end": v(-46, 11) * mm});
            skArc(sketch, "E87.1.0.5", {"start": v(-46, 49) * mm, "mid": v(-46.3, 49.7) * mm, "end": v(-47, 50) * mm});
            skArc(sketch, "E87.1.0.6", {"start": v(-47, 10) * mm, "mid": v(-46.3, 10.3) * mm, "end": v(-46, 11) * mm});
            skArc(sketch, "E87.1.0.7", {"start": v(-48, 11) * mm, "mid": v(-47.7, 10.3) * mm, "end": v(-47, 10) * mm});
            skArc(sketch, "E87.1.0.8", {"start": v(-47, 50) * mm, "mid": v(-47.7, 49.7) * mm, "end": v(-48, 49) * mm});
            skPoint(sketch, "E87.2.0.0", {"position": v(-42, 10) * mm});
            skPoint(sketch, "E87.2.0.1", {"position": v(-44, 10) * mm});
            skPoint(sketch, "E87.2.0.2", {"position": v(-44, 50) * mm});
            skLineSegment(sketch, "E87.2.0.3", {"start": v(-44, 49) * mm, "end": v(-44, 11) * mm});
            skLineSegment(sketch, "E87.2.0.4", {"start": v(-42, 49) * mm, "end": v(-42, 11) * mm});
            skArc(sketch, "E87.2.0.5", {"start": v(-42, 49) * mm, "mid": v(-42.3, 49.7) * mm, "end": v(-43, 50) * mm});
            skArc(sketch, "E87.2.0.6", {"start": v(-43, 10) * mm, "mid": v(-42.3, 10.3) * mm, "end": v(-42, 11) * mm});
            skArc(sketch, "E87.2.0.7", {"start": v(-44, 11) * mm, "mid": v(-43.7, 10.3) * mm, "end": v(-43, 10) * mm});
            skArc(sketch, "E87.2.0.8", {"start": v(-43, 50) * mm, "mid": v(-43.7, 49.7) * mm, "end": v(-44, 49) * mm});
            skPoint(sketch, "E87.3.0.0", {"position": v(-38, 10) * mm});
            skPoint(sketch, "E87.3.0.1", {"position": v(-40, 10) * mm});
            skPoint(sketch, "E87.3.0.2", {"position": v(-40, 50) * mm});
            skLineSegment(sketch, "E87.3.0.3", {"start": v(-40, 49) * mm, "end": v(-40, 11) * mm});
            skLineSegment(sketch, "E87.3.0.4", {"start": v(-38, 49) * mm, "end": v(-38, 11) * mm});
            skArc(sketch, "E87.3.0.5", {"start": v(-38, 49) * mm, "mid": v(-38.3, 49.7) * mm, "end": v(-39, 50) * mm});
            skArc(sketch, "E87.3.0.6", {"start": v(-39, 10) * mm, "mid": v(-38.3, 10.3) * mm, "end": v(-38, 11) * mm});
            skArc(sketch, "E87.3.0.7", {"start": v(-40, 11) * mm, "mid": v(-39.7, 10.3) * mm, "end": v(-39, 10) * mm});
            skArc(sketch, "E87.3.0.8", {"start": v(-39, 50) * mm, "mid": v(-39.7, 49.7) * mm, "end": v(-40, 49) * mm});
            skPoint(sketch, "E87.4.0.0", {"position": v(-34, 10) * mm});
            skPoint(sketch, "E87.4.0.1", {"position": v(-36, 10) * mm});
            skPoint(sketch, "E87.4.0.2", {"position": v(-36, 50) * mm});
            skLineSegment(sketch, "E87.4.0.3", {"start": v(-36, 49) * mm, "end": v(-36, 11) * mm});
            skLineSegment(sketch, "E87.4.0.4", {"start": v(-34, 49) * mm, "end": v(-34, 11) * mm});
            skArc(sketch, "E87.4.0.5", {"start": v(-34, 49) * mm, "mid": v(-34.3, 49.7) * mm, "end": v(-35, 50) * mm});
            skArc(sketch, "E87.4.0.6", {"start": v(-35, 10) * mm, "mid": v(-34.3, 10.3) * mm, "end": v(-34, 11) * mm});
            skArc(sketch, "E87.4.0.7", {"start": v(-36, 11) * mm, "mid": v(-35.7, 10.3) * mm, "end": v(-35, 10) * mm});
            skArc(sketch, "E87.4.0.8", {"start": v(-35, 50) * mm, "mid": v(-35.7, 49.7) * mm, "end": v(-36, 49) * mm});
            skPoint(sketch, "E87.5.0.0", {"position": v(-30, 10) * mm});
            skPoint(sketch, "E87.5.0.1", {"position": v(-32, 10) * mm});
            skPoint(sketch, "E87.5.0.2", {"position": v(-32, 50) * mm});
            skLineSegment(sketch, "E87.5.0.3", {"start": v(-32, 49) * mm, "end": v(-32, 11) * mm});
            skLineSegment(sketch, "E87.5.0.4", {"start": v(-30, 49) * mm, "end": v(-30, 11) * mm});
            skArc(sketch, "E87.5.0.5", {"start": v(-30, 49) * mm, "mid": v(-30.3, 49.7) * mm, "end": v(-31, 50) * mm});
            skArc(sketch, "E87.5.0.6", {"start": v(-31, 10) * mm, "mid": v(-30.3, 10.3) * mm, "end": v(-30, 11) * mm});
            skArc(sketch, "E87.5.0.7", {"start": v(-32, 11) * mm, "mid": v(-31.7, 10.3) * mm, "end": v(-31, 10) * mm});
            skArc(sketch, "E87.5.0.8", {"start": v(-31, 50) * mm, "mid": v(-31.7, 49.7) * mm, "end": v(-32, 49) * mm});
            skLineSegment(sketch, "E87.direction1", {"start": v(-52, 10) * mm, "end": v(-48, 10) * mm, "construction": true});
            skSolve(sketch);
        }
        {
            var Q0;
            Q0=qSketchRegion(id+"F11",true);
            extrude(context, id + "F12", {"entities" : qUnion([Q0]), "operationType" : NewBodyOperationType.REMOVE, "endBound" : BoundingType.UP_TO_NEXT, "oppositeDirection" : true, "depth" : 25 * mm});
        }
        {
            var Q0;
            Q0=makeQuery(id+"F3.opExtrude","CAP_EDGE",EDGE,{"disambiguationData":[OSD([sQuery(id+"F0.wireOp",EDGE,"E21.left")])],"isStart":false});
            var Q1;
            Q1=makeQuery(id+"F3.opExtrude","CAP_EDGE",EDGE,{"disambiguationData":[OSD([sQuery(id+"F0.wireOp",EDGE,"E22.bottom")])],"isStart":false});
            var Q2;
            Q2=makeQuery(id+"F3.opExtrude","CAP_EDGE",EDGE,{"disambiguationData":[OSD([sQuery(id+"F0.wireOp",EDGE,"E21.right")])],"isStart":false});
            var Q3;
            Q3=makeQuery(id+"F3.opExtrude","CAP_EDGE",EDGE,{"disambiguationData":[OSD([sQuery(id+"F0.wireOp",EDGE,"E22.top")])],"isStart":false});
            chamfer(context, id + "F13", {"entities" : qUnion([Q0, Q1, Q2, Q3]), "chamferType" : ChamferType.TWO_OFFSETS, "width1" : 3 * mm, "oppositeDirection" : false, "width2" : 20 * mm, "tangentPropagation" : true});
        }
        {
            var Q0;
            Q0=makeQuery(id+"F3.opExtrude","CAP_EDGE",EDGE,{"disambiguationData":[OSD([sQuery(id+"F0.wireOp",EDGE,"E16.top")])],"isStart":false});
            var Q1;
            Q1=makeQuery(id+"F3.opExtrude","CAP_EDGE",EDGE,{"disambiguationData":[OSD([sQuery(id+"F0.wireOp",EDGE,"E15.left")])],"isStart":false});
            var Q2;
            Q2=makeQuery(id+"F3.opExtrude","CAP_EDGE",EDGE,{"disambiguationData":[OSD([sQuery(id+"F0.wireOp",EDGE,"E15.right")])],"isStart":false});
            var Q3;
            Q3=makeQuery(id+"F3.opExtrude","CAP_EDGE",EDGE,{"disambiguationData":[OSD([sQuery(id+"F0.wireOp",EDGE,"E9.top")])],"isStart":false});
            var Q4;
            Q4=makeQuery(id+"F3.opExtrude","CAP_EDGE",EDGE,{"disambiguationData":[OSD([sQuery(id+"F0.wireOp",EDGE,"E10.right")])],"isStart":false});
            var Q5;
            Q5=makeQuery(id+"F3.opExtrude","CAP_EDGE",EDGE,{"disambiguationData":[OSD([sQuery(id+"F0.wireOp",EDGE,"E27.right")])],"isStart":false});
            var Q6;
            Q6=makeQuery(id+"F3.opExtrude","CAP_EDGE",EDGE,{"disambiguationData":[OSD([sQuery(id+"F0.wireOp",EDGE,"E28.bottom")])],"isStart":false});
            chamfer(context, id + "F14", {"entities" : qUnion([Q0, Q1, Q2, Q3, Q4, Q5, Q6]), "chamferType" : ChamferType.TWO_OFFSETS, "width1" : 20 * mm, "oppositeDirection" : false, "width2" : 3 * mm, "tangentPropagation" : true});
        }
        {
            var Q0;
            Q0=makeQuery(id+"F3.opExtrude","CAP_EDGE",EDGE,{"disambiguationData":[OSD([sQuery(id+"F0.wireOp",EDGE,"E27.left")])],"isStart":false});
            var Q1;
            Q1=makeQuery(id+"F3.opExtrude","CAP_EDGE",EDGE,{"disambiguationData":[OSD([sQuery(id+"F0.wireOp",EDGE,"E28.top")])],"isStart":false});
            var Q2;
            Q2=makeQuery(id+"F3.opExtrude","CAP_EDGE",EDGE,{"disambiguationData":[OSD([sQuery(id+"F0.wireOp",EDGE,"E10.left")])],"isStart":false});
            chamfer(context, id + "F15", {"entities" : qUnion([Q0, Q1, Q2]), "chamferType" : ChamferType.TWO_OFFSETS, "width1" : 3 * mm, "oppositeDirection" : false, "width2" : 20 * mm, "tangentPropagation" : true});
        }
        {
            var Q0;
            {var subQ3=sQuery(id+"F0.wireOp",EDGE,"E35");Q0=makeQuery(id+"F0.imprint","IMPRINT",FACE,{"disambiguationData":[TD([[makeQuery(id+"F0.imprint","IMPRINT",EDGE,{"derivedFrom":subQ3}),-1.0]])]});}
            var Q1;
            {var subQ3=sQuery(id+"F0.wireOp",EDGE,"E36");Q1=makeQuery(id+"F0.imprint","IMPRINT",FACE,{"disambiguationData":[TD([[makeQuery(id+"F0.imprint","IMPRINT",EDGE,{"derivedFrom":subQ3}),-1.0]])]});}
            var Q2;
            {var subQ3=sQuery(id+"F0.wireOp",EDGE,"E34");Q2=makeQuery(id+"F0.imprint","IMPRINT",FACE,{"disambiguationData":[TD([[makeQuery(id+"F0.imprint","IMPRINT",EDGE,{"derivedFrom":subQ3}),1.0]])]});}
            var Q3;
            {var subQ3=sQuery(id+"F0.wireOp",EDGE,"E33");Q3=makeQuery(id+"F0.imprint","IMPRINT",FACE,{"disambiguationData":[TD([[makeQuery(id+"F0.imprint","IMPRINT",EDGE,{"derivedFrom":subQ3}),-1.0]])]});}
            var Q4;
            Q4=makeQuery(id+"F1.opExtrude","CAP_FACE",FACE,{"disambiguationData":[OSD([sQuery(id+"F0.wireOp",EDGE,"E0.bottom"),sQuery(id+"F0.wireOp",EDGE,"E0.top"),sQuery(id+"F0.wireOp",EDGE,"E0.left"),sQuery(id+"F0.wireOp",EDGE,"E0.right")])],"isStart":false});
            extrude(context, id + "F16", {"entities" : qUnion([Q0, Q1, Q2, Q3]), "operationType" : NewBodyOperationType.ADD, "endBound" : BoundingType.UP_TO_SURFACE, "endBoundEntityFace" : qUnion([Q4]), "depth" : 25 * mm});
        }
        {
            var Q0;
            {var subQ0=sQuery(id+"F0.wireOp",EDGE,"E0.right");var subQ1=sQuery(id+"F0.wireOp",EDGE,"E0.top");var subQ2=sQuery(id+"F0.wireOp",EDGE,"E0.left");var subQ3=sQuery(id+"F0.wireOp",EDGE,"E0.bottom");Q0=makeQuery(id+"F16.boolean.opBoolean","MERGE",FACE,{"derivedFrom":[makeQuery(id+"F1.opExtrude","CAP_FACE",FACE,{"disambiguationData":[OSD([subQ3,subQ1,subQ2,subQ0])],"isStart":false}),makeQuery(id+"F16.opExtrude","CAP_FACE",FACE,{"disambiguationData":[OSD([subQ3,subQ1,subQ2,subQ0]),ownerDisambiguation([makeQuery(id+"F16.opExtrude","SWEPT_BODY",BODY,{"disambiguationData":[OSD([subQ3,subQ2,sQuery(id+"F0.wireOp",EDGE,"E34")])]})])],"isStart":false}),makeQuery(id+"F16.opExtrude","CAP_FACE",FACE,{"disambiguationData":[OSD([subQ3,subQ1,subQ2,subQ0]),ownerDisambiguation([makeQuery(id+"F16.opExtrude","SWEPT_BODY",BODY,{"disambiguationData":[OSD([subQ3,subQ0,sQuery(id+"F0.wireOp",EDGE,"E36")])]})])],"isStart":false}),makeQuery(id+"F16.opExtrude","CAP_FACE",FACE,{"disambiguationData":[OSD([subQ3,subQ1,subQ2,subQ0]),ownerDisambiguation([makeQuery(id+"F16.opExtrude","SWEPT_BODY",BODY,{"disambiguationData":[OSD([subQ1,subQ2,sQuery(id+"F0.wireOp",EDGE,"E33")])]})])],"isStart":false}),makeQuery(id+"F16.opExtrude","CAP_FACE",FACE,{"disambiguationData":[OSD([subQ3,subQ1,subQ2,subQ0]),ownerDisambiguation([makeQuery(id+"F16.opExtrude","SWEPT_BODY",BODY,{"disambiguationData":[OSD([subQ1,subQ0,sQuery(id+"F0.wireOp",EDGE,"E35")])]})])],"isStart":false})]});}
            var sketch = newSketch(context, id + "F17", { "sketchPlane" : qUnion([Q0])});
            skCircle(sketch, "E88", {"center": v(-61.9, -71.9) * mm, "radius": 1.45 * mm});
            skCircle(sketch, "E89", {"center": v(-61.9, 71.9) * mm, "radius": 1.45 * mm});
            skCircle(sketch, "E90", {"center": v(61.9, -71.9) * mm, "radius": 1.45 * mm});
            skCircle(sketch, "E91", {"center": v(61.9, 71.9) * mm, "radius": 1.45 * mm});
            skSolve(sketch);
        }
        {
            var Q0;
            Q0=qSketchRegion(id+"F17",true);
            extrude(context, id + "F18", {"entities" : qUnion([Q0]), "operationType" : NewBodyOperationType.REMOVE, "oppositeDirection" : true, "depth" : 15 * mm});
        }
        {
            var Q0;
            {var subQ0=sQuery(id+"F0.wireOp",EDGE,"E0.right");var subQ1=sQuery(id+"F0.wireOp",EDGE,"E0.top");var subQ2=sQuery(id+"F0.wireOp",EDGE,"E0.left");var subQ3=sQuery(id+"F0.wireOp",EDGE,"E0.bottom");Q0=makeQuery(id+"F16.boolean.opBoolean","MERGE",FACE,{"derivedFrom":[makeQuery(id+"F1.opExtrude","CAP_FACE",FACE,{"disambiguationData":[OSD([subQ3,subQ1,subQ2,subQ0])],"isStart":false}),makeQuery(id+"F16.opExtrude","CAP_FACE",FACE,{"disambiguationData":[OSD([subQ3,subQ1,subQ2,subQ0]),ownerDisambiguation([makeQuery(id+"F16.opExtrude","SWEPT_BODY",BODY,{"disambiguationData":[OSD([subQ3,subQ2,sQuery(id+"F0.wireOp",EDGE,"E34")])]})])],"isStart":false}),makeQuery(id+"F16.opExtrude","CAP_FACE",FACE,{"disambiguationData":[OSD([subQ3,subQ1,subQ2,subQ0]),ownerDisambiguation([makeQuery(id+"F16.opExtrude","SWEPT_BODY",BODY,{"disambiguationData":[OSD([subQ3,subQ0,sQuery(id+"F0.wireOp",EDGE,"E36")])]})])],"isStart":false}),makeQuery(id+"F16.opExtrude","CAP_FACE",FACE,{"disambiguationData":[OSD([subQ3,subQ1,subQ2,subQ0]),ownerDisambiguation([makeQuery(id+"F16.opExtrude","SWEPT_BODY",BODY,{"disambiguationData":[OSD([subQ1,subQ2,sQuery(id+"F0.wireOp",EDGE,"E33")])]})])],"isStart":false}),makeQuery(id+"F16.opExtrude","CAP_FACE",FACE,{"disambiguationData":[OSD([subQ3,subQ1,subQ2,subQ0]),ownerDisambiguation([makeQuery(id+"F16.opExtrude","SWEPT_BODY",BODY,{"disambiguationData":[OSD([subQ1,subQ0,sQuery(id+"F0.wireOp",EDGE,"E35")])]})])],"isStart":false})]});}
            var sketch = newSketch(context, id + "F19", { "sketchPlane" : qUnion([Q0])});
            skLineSegment(sketch, "E92.bottom", {"start": v(-65, 75) * mm, "end": v(65, 75) * mm});
            skLineSegment(sketch, "E92.top", {"start": v(-65, -75) * mm, "end": v(65, -75) * mm});
            skLineSegment(sketch, "E92.left", {"start": v(-65, 75) * mm, "end": v(-65, -75) * mm});
            skLineSegment(sketch, "E92.right", {"start": v(65, 75) * mm, "end": v(65, -75) * mm});
            skSolve(sketch);
        }
        {
            var Q0;
            Q0=qSketchRegion(id+"F19",true);
            extrude(context, id + "F20", {"entities" : qUnion([Q0]), "depth" : 2.5 * mm});
        }
        {
            var Q0;
            Q0=makeQuery(id+"F20.opExtrude","SWEPT_BODY",BODY,{"disambiguationData":[OSD([sQuery(id+"F19.wireOp",EDGE,"E92.bottom"),sQuery(id+"F19.wireOp",EDGE,"E92.top"),sQuery(id+"F19.wireOp",EDGE,"E92.left"),sQuery(id+"F19.wireOp",EDGE,"E92.right")])]});
            transform(context, id + "F21", {"entities" : qUnion([Q0]), "transformType" : TransformType.TRANSLATION_3D, "dx" : 0 * mm, "dy" : 0 * mm, "dz" : 75 * mm, "makeCopy" : false});
        }
        {
            var Q0;
            Q0=makeQuery(id+"F20.opExtrude","CAP_FACE",FACE,{"disambiguationData":[OSD([sQuery(id+"F19.wireOp",EDGE,"E92.bottom"),sQuery(id+"F19.wireOp",EDGE,"E92.top"),sQuery(id+"F19.wireOp",EDGE,"E92.left"),sQuery(id+"F19.wireOp",EDGE,"E92.right")])],"isStart":false});
            var sketch = newSketch(context, id + "F22", { "sketchPlane" : qUnion([Q0])});
            skCircle(sketch, "E93", {"center": v(61.9, -71.9) * mm, "radius": 1.6 * mm});
            skCircle(sketch, "E94", {"center": v(-61.9, -71.9) * mm, "radius": 1.6 * mm});
            skCircle(sketch, "E95", {"center": v(-61.9, 71.9) * mm, "radius": 1.6 * mm});
            skCircle(sketch, "E96", {"center": v(61.9, 71.9) * mm, "radius": 1.6 * mm});
            skCircle(sketch, "E97", {"center": v(-61.9, -71.9) * mm, "radius": 2.75 * mm});
            skCircle(sketch, "E98", {"center": v(61.9, -71.9) * mm, "radius": 2.75 * mm});
            skCircle(sketch, "E99", {"center": v(61.9, 71.9) * mm, "radius": 2.75 * mm});
            skCircle(sketch, "E100", {"center": v(-61.9, 71.9) * mm, "radius": 2.75 * mm});
            skSolve(sketch);
        }
        {
            var Q0;
            Q0=makeQuery(id+"F22.imprint","IMPRINT",FACE,{"disambiguationData":[TD([[makeQuery(id+"F22.imprint","IMPRINT",EDGE,{"derivedFrom":sQuery(id+"F22.wireOp",EDGE,"E94")}),1.0]])]});
            var Q1;
            Q1=makeQuery(id+"F22.imprint","IMPRINT",FACE,{"disambiguationData":[TD([[makeQuery(id+"F22.imprint","IMPRINT",EDGE,{"derivedFrom":sQuery(id+"F22.wireOp",EDGE,"E93")}),1.0]])]});
            var Q2;
            Q2=makeQuery(id+"F22.imprint","IMPRINT",FACE,{"disambiguationData":[TD([[makeQuery(id+"F22.imprint","IMPRINT",EDGE,{"derivedFrom":sQuery(id+"F22.wireOp",EDGE,"E96")}),1.0]])]});
            var Q3;
            Q3=makeQuery(id+"F22.imprint","IMPRINT",FACE,{"disambiguationData":[TD([[makeQuery(id+"F22.imprint","IMPRINT",EDGE,{"derivedFrom":sQuery(id+"F22.wireOp",EDGE,"E95")}),1.0]])]});
            extrude(context, id + "F23", {"entities" : qUnion([Q0, Q1, Q2, Q3]), "operationType" : NewBodyOperationType.REMOVE, "endBound" : BoundingType.UP_TO_NEXT, "oppositeDirection" : true, "depth" : 25 * mm});
        }
        {
            var Q0;
            Q0=makeQuery(id+"F1.opExtrude","SWEPT_EDGE",EDGE,{"disambiguationData":[OSD([sQuery(id+"F0.wireOp",EDGE,"E0.bottom"),sQuery(id+"F0.wireOp",EDGE,"E0.left")])]});
            var Q1;
            Q1=makeQuery(id+"F1.opExtrude","SWEPT_EDGE",EDGE,{"disambiguationData":[OSD([sQuery(id+"F0.wireOp",EDGE,"E0.bottom"),sQuery(id+"F0.wireOp",EDGE,"E0.right")])]});
            var Q2;
            Q2=makeQuery(id+"F1.opExtrude","SWEPT_EDGE",EDGE,{"disambiguationData":[OSD([sQuery(id+"F0.wireOp",EDGE,"E0.top"),sQuery(id+"F0.wireOp",EDGE,"E0.left")])]});
            var Q3;
            Q3=makeQuery(id+"F1.opExtrude","SWEPT_EDGE",EDGE,{"disambiguationData":[OSD([sQuery(id+"F0.wireOp",EDGE,"E0.top"),sQuery(id+"F0.wireOp",EDGE,"E0.right")])]});
            var Q4;
            Q4=makeQuery(id+"F1.opExtrude","CAP_EDGE",EDGE,{"disambiguationData":[OSD([sQuery(id+"F0.wireOp",EDGE,"E0.right")])],"isStart":true});
            var Q5;
            Q5=makeQuery(id+"F20.opExtrude","SWEPT_EDGE",EDGE,{"disambiguationData":[OSD([sQuery(id+"F19.wireOp",EDGE,"E92.top"),sQuery(id+"F19.wireOp",EDGE,"E92.right")])]});
            var Q6;
            Q6=makeQuery(id+"F20.opExtrude","SWEPT_EDGE",EDGE,{"disambiguationData":[OSD([sQuery(id+"F19.wireOp",EDGE,"E92.bottom"),sQuery(id+"F19.wireOp",EDGE,"E92.right")])]});
            var Q7;
            Q7=makeQuery(id+"F20.opExtrude","SWEPT_EDGE",EDGE,{"disambiguationData":[OSD([sQuery(id+"F19.wireOp",EDGE,"E92.bottom"),sQuery(id+"F19.wireOp",EDGE,"E92.left")])]});
            var Q8;
            Q8=makeQuery(id+"F20.opExtrude","SWEPT_EDGE",EDGE,{"disambiguationData":[OSD([sQuery(id+"F19.wireOp",EDGE,"E92.top"),sQuery(id+"F19.wireOp",EDGE,"E92.left")])]});
            fillet(context, id + "F24", {"entities" : qUnion([Q0, Q1, Q2, Q3, Q4, Q5, Q6, Q7, Q8]), "radius" : 1 * mm, "tangentPropagation" : true, "allowEdgeOverflow" : false});
        }
        {
            var Q0;
            Q0=makeQuery(id+"F1.opExtrude","SWEPT_FACE",FACE,{"disambiguationData":[OSD([sQuery(id+"F0.wireOp",EDGE,"E0.bottom")])]});
            cPlane(context, id + "F25", {"entities" : qUnion([Q0]), "cplaneType" : CPlaneType.OFFSET, "offset" : 22 * mm, "oppositeDirection" : true, "width" : 150 * mm, "height" : 150 * mm});
        }
        {
            var Q0;
            Q0=qCreatedBy(id+"F25.planeOp",FACE);
            var sketch = newSketch(context, id + "F26", { "sketchPlane" : qUnion([Q0])});
            skArc(sketch, "E101", {"start": v(53, 30) * mm, "mid": v(33, 50) * mm, "end": v(13, 30) * mm, "construction": true});
            skEllipse(sketch, "E102", {"center": v(33, 19.5) * mm, "majorRadius": 18 * mm, "minorRadius": 3 * mm, "majorAxis": v(-1, 0)});
            skLineSegment(sketch, "E103", {"start": v(53, 30) * mm, "end": v(13, 30) * mm, "construction": true});
            skLineSegment(sketch, "E104", {"start": v(51, 19.5) * mm, "end": v(15, 19.5) * mm});
            skEllipse(sketch, "E105", {"center": v(33, 19.5) * mm, "majorRadius": 17 * mm, "minorRadius": 2 * mm, "majorAxis": v(-1, 0)});
            skSolve(sketch);
        }
        {
            var Q0;
            Q0=makeQuery(id+"F1.opExtrude","SWEPT_FACE",FACE,{"disambiguationData":[OSD([sQuery(id+"F0.wireOp",EDGE,"E0.bottom")])]});
            cPlane(context, id + "F27", {"entities" : qUnion([Q0]), "cplaneType" : CPlaneType.OFFSET, "offset" : (10 + 2.5 + 2) * mm, "oppositeDirection" : true, "width" : 150 * mm, "height" : 150 * mm});
        }
        {
            var Q0;
            Q0=qCreatedBy(id+"F27.planeOp",FACE);
            var sketch = newSketch(context, id + "F28", { "sketchPlane" : qUnion([Q0])});
            skArc(sketch, "E106", {"start": v(53, 30) * mm, "mid": v(33, 50) * mm, "end": v(13, 30) * mm});
            skLineSegment(sketch, "E107", {"start": v(53, 30) * mm, "end": v(52, 30) * mm});
            skPoint(sketch, "E108.orphan", {"position": v(58.06, 30) * mm});
            skArc(sketch, "E109.0", {"start": v(52, 30) * mm, "mid": v(33, 49) * mm, "end": v(14, 30) * mm});
            skLineSegment(sketch, "E110.trimOffspring", {"start": v(14, 30) * mm, "end": v(13, 30) * mm});
            skSolve(sketch);
        }
        {
            var Q1;
            {var subQ0=sQuery(id+"F28.wireOp",EDGE,"E106");Q1=makeQuery(id+"F28.imprint","IMPRINT",FACE,{"disambiguationData":[TD([[makeQuery(id+"F28.imprint","IMPRINT",EDGE,{"derivedFrom":subQ0}),1.0]])]});}
            var Q2;
            {var subQ0=sQuery(id+"F26.wireOp",EDGE,"E104");Q2=makeQuery(id+"F26.imprint","IMPRINT",FACE,{"disambiguationData":[TD([[makeQuery(id+"F26.imprint","IMPRINT",EDGE,{"derivedFrom":subQ0}),-1.0]])]});}
            loft(context, id + "F29", {"operationType" : NewBodyOperationType.ADD, "sheetProfilesArray" : [{ "sheetProfileEntities" : qUnion([Q1]) }, { "sheetProfileEntities" : qUnion([Q2]) }]});
        }
        {
            var Q0;
            Q0=qCreatedBy(id+"F27.planeOp",FACE);
            var sketch = newSketch(context, id + "F30", { "sketchPlane" : qUnion([Q0])});
            skCircle(sketch, "E111", {"center": v(49, 46) * mm, "radius": 2.15 * mm});
            skCircle(sketch, "E112", {"center": v(17, 46) * mm, "radius": 2.15 * mm});
            skCircle(sketch, "E113", {"center": v(33, 30) * mm, "radius": 19 * mm});
            skLineSegment(sketch, "E114.bottom", {"start": v(49, 14) * mm, "end": v(17, 14) * mm});
            skLineSegment(sketch, "E114.top", {"start": v(49, 46) * mm, "end": v(17, 46) * mm});
            skLineSegment(sketch, "E114.left", {"start": v(49, 14) * mm, "end": v(49, 46) * mm});
            skLineSegment(sketch, "E114.right", {"start": v(17, 14) * mm, "end": v(17, 46) * mm});
            skLineSegment(sketch, "E115.bottom", {"start": v(53, 50) * mm, "end": v(13, 50) * mm});
            skLineSegment(sketch, "E115.top", {"start": v(53, 10) * mm, "end": v(13, 10) * mm});
            skLineSegment(sketch, "E115.left", {"start": v(53, 50) * mm, "end": v(53, 10) * mm});
            skLineSegment(sketch, "E115.right", {"start": v(13, 50) * mm, "end": v(13, 10) * mm});
            skCircle(sketch, "E116", {"center": v(17, 14) * mm, "radius": 2.15 * mm});
            skCircle(sketch, "E117", {"center": v(49, 14) * mm, "radius": 2.15 * mm});
            skPoint(sketch, "E118.startSnap0", {"position": v(49, 30) * mm});
            skSolve(sketch);
        }
        {
            var Q0;
            Q0=makeQuery(id+"F30.imprint","IMPRINT",FACE,{"disambiguationData":[TD([[makeQuery(id+"F30.imprint","IMPRINT",EDGE,{"derivedFrom":sQuery(id+"F30.wireOp",EDGE,"E115.bottom")}),1.0]])]});
            var Q1;
            {var subQ0=sQuery(id+"F30.wireOp",EDGE,"E114.top");var subQ1=sQuery(id+"F30.wireOp",EDGE,"E112");var subQ2=makeQuery(id+"F30.imprint","INTERSECT",VERTEX,{"derivedFrom":[subQ1,subQ0]});Q1=makeQuery(id+"F30.imprint","IMPRINT",FACE,{"disambiguationData":[TD([[makeQuery(id+"F30.imprint","IMPRINT",EDGE,{"disambiguationData":[TD([[subQ2,1.0]])],"derivedFrom":subQ1}),-1.0]])]});}
            var Q2;
            {var subQ0=sQuery(id+"F30.wireOp",EDGE,"E114.top");var subQ1=sQuery(id+"F30.wireOp",EDGE,"E111");var subQ2=makeQuery(id+"F30.imprint","INTERSECT",VERTEX,{"derivedFrom":[subQ1,subQ0]});Q2=makeQuery(id+"F30.imprint","IMPRINT",FACE,{"disambiguationData":[TD([[makeQuery(id+"F30.imprint","IMPRINT",EDGE,{"disambiguationData":[TD([[subQ2,-1.0]])],"derivedFrom":subQ1}),-1.0]])]});}
            var Q3;
            {var subQ0=sQuery(id+"F30.wireOp",EDGE,"E114.bottom");var subQ1=sQuery(id+"F30.wireOp",EDGE,"E113");var subQ2=makeQuery(id+"F30.imprint","INTERSECT",VERTEX,{"disambiguationData":[OD(1.0)],"derivedFrom":[subQ1,subQ0]});Q3=makeQuery(id+"F30.imprint","IMPRINT",FACE,{"disambiguationData":[TD([[makeQuery(id+"F30.imprint","IMPRINT",EDGE,{"disambiguationData":[TD([[subQ2,-1.0]])],"derivedFrom":subQ1}),-1.0]])]});}
            var Q4;
            {var subQ0=sQuery(id+"F30.wireOp",EDGE,"E114.right");var subQ1=sQuery(id+"F30.wireOp",EDGE,"E113");var subQ2=makeQuery(id+"F30.imprint","INTERSECT",VERTEX,{"disambiguationData":[OD(1.0)],"derivedFrom":[subQ1,subQ0]});Q4=makeQuery(id+"F30.imprint","IMPRINT",FACE,{"disambiguationData":[TD([[makeQuery(id+"F30.imprint","IMPRINT",EDGE,{"disambiguationData":[TD([[subQ2,-1.0]])],"derivedFrom":subQ1}),-1.0]])]});}
            extrude(context, id + "F31", {"entities" : qUnion([Q0, Q1, Q2, Q3, Q4]), "operationType" : NewBodyOperationType.ADD, "depth" : 2 * mm});
        }
        {
            var Q0;
            Q0=makeQuery(id+"F29.opLoft","SWEPT_FACE",FACE,{"disambiguationData":[OSD([sQuery(id+"F26.wireOp",EDGE,"E102"),sQuery(id+"F26.wireOp",EDGE,"E104"),sQuery(id+"F26.wireOp",EDGE,"E105"),sQuery(id+"F28.wireOp",EDGE,"E106"),sQuery(id+"F28.wireOp",EDGE,"E109.0"),sQuery(id+"F28.wireOp",EDGE,"E110.trimOffspring")])]});
            var Q1;
            Q1=makeQuery(id+"F29.opLoft","SWEPT_FACE",FACE,{"disambiguationData":[OSD([sQuery(id+"F26.wireOp",EDGE,"E102"),sQuery(id+"F26.wireOp",EDGE,"E104"),sQuery(id+"F26.wireOp",EDGE,"E105"),sQuery(id+"F28.wireOp",EDGE,"E106"),sQuery(id+"F28.wireOp",EDGE,"E107"),sQuery(id+"F28.wireOp",EDGE,"E109.0")])]});
            var Q2;
            Q2=makeQuery(id+"F31.opExtrude","SWEPT_FACE",FACE,{"disambiguationData":[OSD([sQuery(id+"F30.wireOp",EDGE,"E115.top")])]});
            var Q3;
            {var subQ0=sQuery(id+"F30.wireOp",EDGE,"E115.right");var subQ1=sQuery(id+"F30.wireOp",EDGE,"E115.left");var subQ2=sQuery(id+"F30.wireOp",EDGE,"E113");var subQ3=sQuery(id+"F30.wireOp",EDGE,"E117");var subQ4=sQuery(id+"F30.wireOp",EDGE,"E116");var subQ5=sQuery(id+"F30.wireOp",EDGE,"E115.top");var subQ6=makeQuery(id+"F31.opExtrude","CAP_FACE",FACE,{"disambiguationData":[OSD([sQuery(id+"F30.wireOp",EDGE,"E111"),sQuery(id+"F30.wireOp",EDGE,"E112"),subQ2,sQuery(id+"F30.wireOp",EDGE,"E115.bottom"),subQ5,subQ1,subQ0,subQ4,subQ3])],"isStart":true});Q3=makeQuery(id+"F31.boolean.opBoolean","SPLIT",FACE,{"disambiguationData":[TD([makeQuery(id+"F31.opExtrude","SWEPT_FACE",FACE,{"disambiguationData":[OSD([subQ2])]})])],"derivedFrom":subQ6});}
            var Q4;
            {var subQ0=sQuery(id+"F26.wireOp",EDGE,"E104");var subQ1=sQuery(id+"F26.wireOp",EDGE,"E102");var subQ2=makeQuery(id+"F26.imprint","INTERSECT",VERTEX,{"disambiguationData":[OD(0.0)],"derivedFrom":[subQ1,subQ0]});Q4=makeQuery(id+"F29.opLoft","SWEPT_BODY",BODY,{"disambiguationData":[OSD([makeQuery(id+"F26.imprint","IMPRINT",FACE,{"disambiguationData":[TD([[makeQuery(id+"F26.imprint","IMPRINT",EDGE,{"disambiguationData":[TD([[subQ2,-1.0]])],"derivedFrom":subQ1}),1.0]])]}),makeQuery(id+"F28.imprint","IMPRINT",FACE,{"disambiguationData":[TD([[makeQuery(id+"F28.imprint","IMPRINT",EDGE,{"derivedFrom":sQuery(id+"F28.wireOp",EDGE,"E106")}),1.0]])]})])]});}
            var Q5;
            Q5=makeQuery(id+"F31.opExtrude","CAP_VERTEX",VERTEX,{"disambiguationData":[OSD([sQuery(id+"F30.wireOp",EDGE,"E115.top"),sQuery(id+"F30.wireOp",EDGE,"E115.left")])],"isStart":false});
            extrude(context, id + "F32", {"entities" : qUnion([Q0, Q1]), "operationType" : NewBodyOperationType.ADD, "endBound" : BoundingType.UP_TO_SURFACE, "endBoundEntityFace" : qUnion([Q2]), "depth" : 25 * mm});
        }
        {
            var Q0;
            Q0=makeQuery(id+"F31.opExtrude","SWEPT_FACE",FACE,{"disambiguationData":[OSD([sQuery(id+"F30.wireOp",EDGE,"E115.right")])]});
            var sketch = newSketch(context, id + "F33", { "sketchPlane" : qUnion([Q0])});
            skLineSegment(sketch, "E119.bottom", {"start": v(62.5, 10) * mm, "end": v(92.5, 10) * mm});
            skLineSegment(sketch, "E119.top", {"start": v(62.5, 50) * mm, "end": v(92.5, 50) * mm});
            skLineSegment(sketch, "E119.left", {"start": v(62.5, 10) * mm, "end": v(62.5, 50) * mm});
            skLineSegment(sketch, "E119.right", {"start": v(92.5, 10) * mm, "end": v(92.5, 50) * mm});
            skSolve(sketch);
        }
        {
            var Q0;
            {var subQ1=sQuery(id+"F33.wireOp",EDGE,"E119.bottom");Q0=makeQuery(id+"F33.imprint","IMPRINT",FACE,{"disambiguationData":[TD([[makeQuery(id+"F33.imprint","IMPRINT",EDGE,{"derivedFrom":subQ1}),1.0]])]});}
            var Q1;
            Q1=makeQuery(id+"F31.opExtrude","SWEPT_FACE",FACE,{"disambiguationData":[OSD([sQuery(id+"F30.wireOp",EDGE,"E115.left")])]});
            extrude(context, id + "F34", {"entities" : qUnion([Q0]), "operationType" : NewBodyOperationType.REMOVE, "endBound" : BoundingType.UP_TO_SURFACE, "oppositeDirection" : true, "endBoundEntityFace" : qUnion([Q1]), "depth" : 25 * mm});
        }
        {
            var Q0;
            Q0=makeQuery(id+"F31.opExtrude","SWEPT_EDGE",EDGE,{"disambiguationData":[OSD([sQuery(id+"F30.wireOp",EDGE,"E115.bottom"),sQuery(id+"F30.wireOp",EDGE,"E115.right")])]});
            var Q1;
            Q1=makeQuery(id+"F31.opExtrude","SWEPT_EDGE",EDGE,{"disambiguationData":[OSD([sQuery(id+"F30.wireOp",EDGE,"E115.bottom"),sQuery(id+"F30.wireOp",EDGE,"E115.left")])]});
            var Q2;
            Q2=makeQuery(id+"F31.opExtrude","SWEPT_EDGE",EDGE,{"disambiguationData":[OSD([sQuery(id+"F30.wireOp",EDGE,"E115.top"),sQuery(id+"F30.wireOp",EDGE,"E115.right")])]});
            var Q3;
            Q3=makeQuery(id+"F31.opExtrude","SWEPT_EDGE",EDGE,{"disambiguationData":[OSD([sQuery(id+"F30.wireOp",EDGE,"E115.top"),sQuery(id+"F30.wireOp",EDGE,"E115.left")])]});
            fillet(context, id + "F35", {"entities" : qUnion([Q0, Q1, Q2, Q3]), "radius" : 5 * mm, "tangentPropagation" : true, "allowEdgeOverflow" : false});
        }
    });
